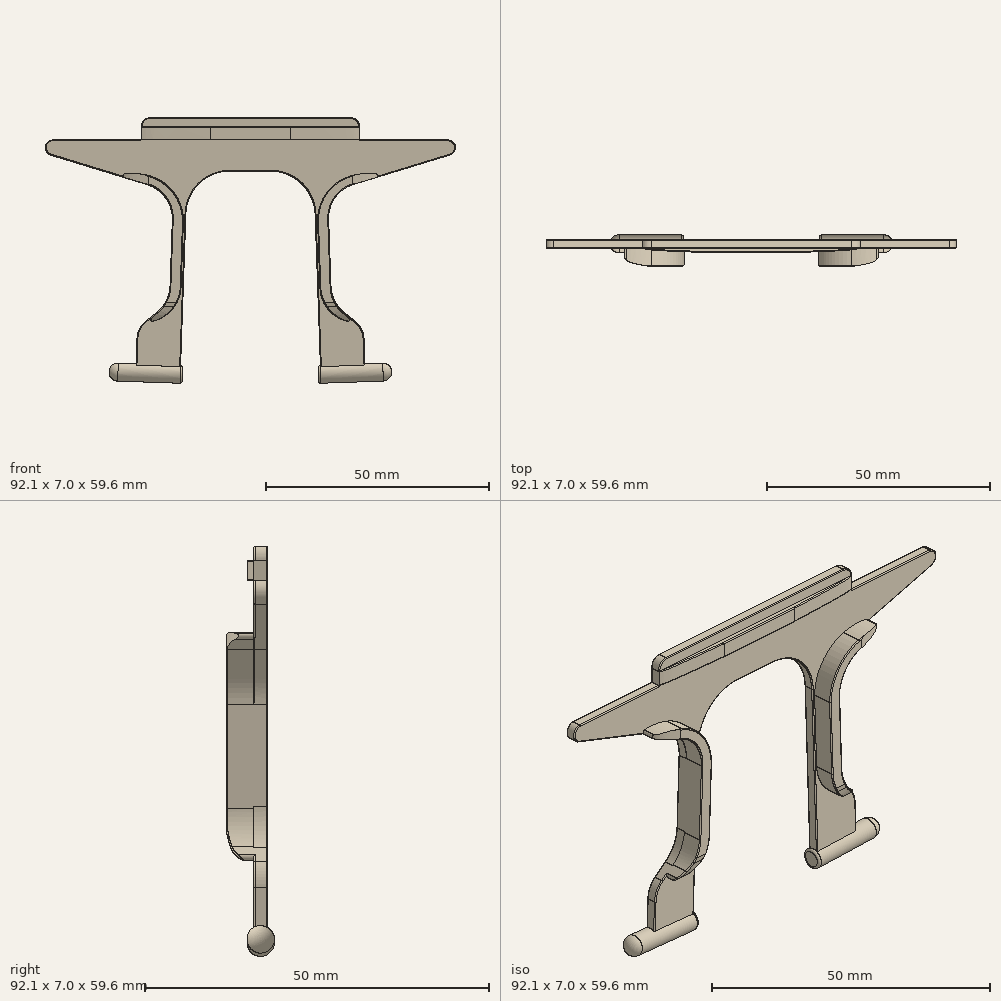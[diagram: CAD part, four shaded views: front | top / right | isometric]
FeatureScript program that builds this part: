
annotation { "Feature Type Name" : "Feature", "Feature Type Description" : "" }
export const myFeature = defineFeature(function(context is Context, id is Id, definition is map)
    precondition{}
    {
        {
            var Q0;
            Q0=qCreatedBy(makeId("Front.planeOp"),FACE);
            var sketch = newSketch(context, id + "F0", { "sketchPlane" : qUnion([Q0])});
            skLineSegment(sketch, "E0", {"start": v(24.5, 40.36) * mm, "end": v(44.5, 40.36) * mm});
            skLineSegment(sketch, "E1", {"start": v(0, 45.36) * mm, "end": v(22.5, 45.36) * mm});
            skLineSegment(sketch, "E2", {"start": v(24.5, 43.36) * mm, "end": v(24.5, 40.36) * mm});
            skPoint(sketch, "E3.visualSharp", {"position": v(24.5, 45.36) * mm});
            skArc(sketch, "E3.filletArc", {"start": v(24.5, 43.36) * mm, "mid": v(23.91, 44.77) * mm, "end": v(22.5, 45.36) * mm});
            skArc(sketch, "E4", {"start": v(44.8, 36.95) * mm, "mid": v(46, 38.99) * mm, "end": v(44.07, 40.36) * mm});
            skLineSegment(sketch, "E5", {"start": v(15.76, -12.27) * mm, "end": v(14.5, 23.7) * mm});
            skLineSegment(sketch, "E6", {"start": v(4.51, 33.36) * mm, "end": v(0, 33.36) * mm});
            skLineSegment(sketch, "E7", {"start": v(44.8, 36.95) * mm, "end": v(23.2, 30.35) * mm});
            skLineSegment(sketch, "E8", {"start": v(25.76, -11.92) * mm, "end": v(25.49, -4.2) * mm});
            skPoint(sketch, "E9.visualSharp", {"position": v(14.17, 33.36) * mm});
            skArc(sketch, "E9.filletArc", {"start": v(14.5, 23.7) * mm, "mid": v(11.46, 30.55) * mm, "end": v(4.51, 33.36) * mm});
            skLineSegment(sketch, "E10", {"start": v(25.76, -11.92) * mm, "end": v(15.76, -12.27) * mm});
            skPoint(sketch, "E11.MirrorCS.start.orphan", {"position": v(0, 45.36) * mm});
            skPoint(sketch, "E12.MirrorCS.end.orphan", {"position": v(0, 33.36) * mm});
            skLineSegment(sketch, "E13", {"start": v(0, 45.36) * mm, "end": v(0, 33.36) * mm});
            skLineSegment(sketch, "E14", {"start": v(18.06, 7.74) * mm, "end": v(17.55, 22.42) * mm});
            skPoint(sketch, "E15.visualSharp", {"position": v(17.34, 28.56) * mm});
            skArc(sketch, "E15.filletArc", {"start": v(23.2, 30.35) * mm, "mid": v(19.03, 27.35) * mm, "end": v(17.55, 22.42) * mm});
            skLineSegment(sketch, "E16", {"start": v(18.06, 7.74) * mm, "end": v(18.07, 7.54) * mm});
            skLineSegment(sketch, "E17", {"start": v(23.63, -0.5) * mm, "end": v(21.04, 1.6) * mm});
            skPoint(sketch, "E18.visualSharp", {"position": v(18.2, 3.9) * mm});
            skArc(sketch, "E18.filletArc", {"start": v(18.07, 7.54) * mm, "mid": v(18.9, 4.25) * mm, "end": v(21.04, 1.6) * mm});
            skPoint(sketch, "E19.visualSharp", {"position": v(25.4, -1.93) * mm});
            skArc(sketch, "E19.filletArc", {"start": v(25.49, -4.2) * mm, "mid": v(24.96, -2.15) * mm, "end": v(23.63, -0.5) * mm});
            skSolve(sketch);
        }
        {
            var Q0;
            Q0=makeQuery(id+"F0.imprint","IMPRINT",FACE,{"disambiguationData":[TD([[makeQuery(id+"F0.imprint","IMPRINT",EDGE,{"derivedFrom":sQuery(id+"F0.wireOp",EDGE,"E1")}),-1.0]])]});
            extrude(context, id + "F1", {"entities" : qUnion([Q0]), "depth" : 1 * mm});
        }
        {
            var Q0;
            Q0=makeQuery(id+"F1.opExtrude","SWEPT_FACE",FACE,{"disambiguationData":[OSD([sQuery(id+"F0.wireOp",EDGE,"E5")])]});
            cPlane(context, id + "F2", {"entities" : qUnion([Q0]), "cplaneType" : CPlaneType.OFFSET, "offset" : 1 * mm, "width" : 150 * mm, "height" : 150 * mm});
        }
        {
            var Q0;
            Q0=makeQuery(id+"F0.imprint","IMPRINT",FACE,{"disambiguationData":[TD([[makeQuery(id+"F0.imprint","IMPRINT",EDGE,{"derivedFrom":sQuery(id+"F0.wireOp",EDGE,"E1")}),-1.0]])]});
            extrude(context, id + "F3", {"entities" : qUnion([Q0]), "operationType" : NewBodyOperationType.ADD, "oppositeDirection" : true, "depth" : 1 * mm});
        }
        {
            var Q0;
            Q0=qCreatedBy(makeId("Front.planeOp"),FACE);
            var sketch = newSketch(context, id + "F4", { "sketchPlane" : qUnion([Q0])});
            skLineSegment(sketch, "E20.bottom", {"start": v(15.7, -10.27) * mm, "end": v(29.68, -9.79) * mm});
            skLineSegment(sketch, "E20.top", {"start": v(15.26, -12.29) * mm, "end": v(31.75, -11.71) * mm});
            skLineSegment(sketch, "E20.left", {"start": v(15.2, -10.8) * mm, "end": v(15.26, -12.29) * mm});
            skLineSegment(sketch, "E20.right", {"start": v(31.75, -11.71) * mm, "end": v(31.75, -11.71) * mm});
            skPoint(sketch, "E21.visualSharp", {"position": v(31.68, -9.72) * mm});
            skArc(sketch, "E21.filletArc", {"start": v(31.75, -11.71) * mm, "mid": v(31.12, -10.32) * mm, "end": v(29.68, -9.79) * mm});
            skPoint(sketch, "E22.visualSharp", {"position": v(15.2, -10.3) * mm});
            skArc(sketch, "E22.filletArc", {"start": v(15.7, -10.27) * mm, "mid": v(15.34, -10.43) * mm, "end": v(15.2, -10.8) * mm});
            skSolve(sketch);
        }
        {
            var Q0;
            Q0=makeQuery(id+"F4.imprint","IMPRINT",FACE,{"disambiguationData":[TD([[makeQuery(id+"F4.imprint","IMPRINT",EDGE,{"derivedFrom":sQuery(id+"F4.wireOp",EDGE,"E20.bottom")}),-1.0]])]});
            var Q1;
            Q1=sQuery(id+"F4.wireOp",EDGE,"E20.top");
            revolve(context, id + "F5", {"operationType" : NewBodyOperationType.ADD, "entities" : qUnion([Q0]), "axis" : qUnion([Q1]), "revolveType" : RevolveType.FULL});
        }
        {
            var Q0;
            Q0=qCreatedBy(makeId("Front.planeOp"),FACE);
            var sketch = newSketch(context, id + "F6", { "sketchPlane" : qUnion([Q0])});
            skLineSegment(sketch, "E23", {"start": v(27.99, 31.83) * mm, "end": v(23.2, 30.37) * mm});
            skLineSegment(sketch, "E24", {"start": v(17.9, 12.5) * mm, "end": v(17.55, 22.44) * mm});
            skArc(sketch, "E25.filletArc", {"start": v(23.2, 30.37) * mm, "mid": v(19.03, 27.36) * mm, "end": v(17.55, 22.44) * mm});
            skLineSegment(sketch, "E26", {"start": v(17.9, 12.5) * mm, "end": v(18.08, 7.32) * mm});
            skLineSegment(sketch, "E27", {"start": v(22.33, 0.55) * mm, "end": v(20.86, 1.75) * mm});
            skArc(sketch, "E28.filletArc", {"start": v(18.08, 7.32) * mm, "mid": v(18.86, 4.23) * mm, "end": v(20.86, 1.75) * mm});
            skLineSegment(sketch, "E29", {"start": v(15.05, 22.35) * mm, "end": v(15.58, 7.23) * mm});
            skLineSegment(sketch, "E30", {"start": v(17.55, 22.44) * mm, "end": v(15.05, 22.35) * mm});
            skLineSegment(sketch, "E31", {"start": v(22.5, 32.26) * mm, "end": v(22.5, 32.26) * mm});
            skLineSegment(sketch, "E32", {"start": v(15.07, 21.85) * mm, "end": v(15.05, 22.35) * mm});
            skArc(sketch, "E33.filletArc", {"start": v(22.5, 32.26) * mm, "mid": v(17.02, 28.32) * mm, "end": v(15.07, 21.85) * mm});
            skLineSegment(sketch, "E34", {"start": v(18.08, 7.32) * mm, "end": v(15.58, 7.23) * mm});
            skLineSegment(sketch, "E35", {"start": v(15.58, 7.23) * mm, "end": v(15.59, 7) * mm});
            skArc(sketch, "E36", {"start": v(15.58, 7.23) * mm, "mid": v(17.44, 2.35) * mm, "end": v(21.9, -0.37) * mm});
            skArc(sketch, "E37", {"start": v(21.9, -0.37) * mm, "mid": v(22.48, -0.08) * mm, "end": v(22.33, 0.55) * mm});
            skPoint(sketch, "E37.first.point", {"position": v(22.45, -0.13) * mm});
            skArc(sketch, "E38.trimOffspring", {"start": v(28.16, 32.74) * mm, "mid": v(25.3, 32.8) * mm, "end": v(22.5, 32.26) * mm});
            skLineSegment(sketch, "E39", {"start": v(27.99, 31.83) * mm, "end": v(28.23, 31.9) * mm});
            skArc(sketch, "E40", {"start": v(28.23, 31.9) * mm, "mid": v(28.54, 32.35) * mm, "end": v(28.16, 32.74) * mm});
            skPoint(sketch, "E40.second.point", {"position": v(28.23, 31.9) * mm});
            skSolve(sketch);
        }
        {
            var Q0;
            Q0 = qSketchRegion(id + "F6", true);
            extrude(context, id + "F7", {"entities" : qUnion([Q0]), "operationType" : NewBodyOperationType.ADD, "depth" : 5 * mm});
        }
        {
            var Q0;
            Q0=qCreatedBy(makeId("Right.planeOp"),FACE);
            var sketch = newSketch(context, id + "F8", { "sketchPlane" : qUnion([Q0])});
            skFitSpline(sketch, "E41", {"points": [v(-4.8, 2.94) * mm, v(-3.88, 0.66) * mm, v(-2.13, -0.5) * mm], "startDerivative": vector(1.29, -4.9) * mm, "endDerivative": vector(4.1, -1.93) * mm});
            skLineSegment(sketch, "E42", {"start": v(-4.8, 2.94) * mm, "end": v(-5.4, 5.71) * mm});
            skLineSegment(sketch, "E43", {"start": v(-5.4, 5.71) * mm, "end": v(-6.33, 5.51) * mm});
            skLineSegment(sketch, "E44", {"start": v(-6.33, 5.51) * mm, "end": v(-6.33, 2.04) * mm});
            skLineSegment(sketch, "E45", {"start": v(-6.33, 2.04) * mm, "end": v(-6.33, -1.36) * mm});
            skLineSegment(sketch, "E46", {"start": v(-6.33, -1.36) * mm, "end": v(-2.06, -1.36) * mm});
            skLineSegment(sketch, "E47", {"start": v(-2.06, -1.36) * mm, "end": v(-2.13, -0.5) * mm});
            skSolve(sketch);
        }
        {
            var Q0;
            Q0=makeQuery(id+"F8.imprint","IMPRINT",FACE,{"disambiguationData":[TD([[makeQuery(id+"F8.imprint","IMPRINT",EDGE,{"derivedFrom":sQuery(id+"F8.wireOp",EDGE,"E41")}),-1.0]])]});
            extrude(context, id + "F9", {"entities" : qUnion([Q0]), "operationType" : NewBodyOperationType.REMOVE, "depth" : 25 * mm});
        }
        {
            var Q0;
            Q0=qCreatedBy(makeId("Top.planeOp"),FACE);
            var sketch = newSketch(context, id + "F10", { "sketchPlane" : qUnion([Q0])});
            skFitSpline(sketch, "E48", {"points": [v(28.64, -3.11) * mm, v(26.82, -4.28) * mm, v(21.34, -5.17) * mm, v(21.32, -5.17) * mm], "startDerivative": vector(-3.06, -3.38) * mm, "endDerivative": vector(-0.28, 0.04) * mm});
            skLineSegment(sketch, "E49", {"start": v(21.34, -5.17) * mm, "end": v(21.34, -6.23) * mm});
            skLineSegment(sketch, "E50", {"start": v(21.34, -6.23) * mm, "end": v(29, -6.23) * mm});
            skLineSegment(sketch, "E51", {"start": v(29, -6.23) * mm, "end": v(29.97, -3.8) * mm});
            skLineSegment(sketch, "E52", {"start": v(29.97, -3.8) * mm, "end": v(29.39, -3.18) * mm});
            skLineSegment(sketch, "E53", {"start": v(29.39, -3.18) * mm, "end": v(28.64, -3.11) * mm});
            skSolve(sketch);
        }
        {
            var Q0;
            {var subQ0=sQuery(id+"F10.wireOp",EDGE,"E49");Q0=makeQuery(id+"F10.imprint","IMPRINT",FACE,{"disambiguationData":[TD([[makeQuery(id+"F10.imprint","IMPRINT",EDGE,{"derivedFrom":subQ0}),1.0]])]});}
            extrude(context, id + "F11", {"entities" : qUnion([Q0]), "operationType" : NewBodyOperationType.REMOVE, "depth" : 35 * mm});
        }
        {
            var Q0;
            Q0=makeQuery(id+"F7.opExtrude","CAP_EDGE",EDGE,{"disambiguationData":[OSD([sQuery(id+"F6.wireOp",EDGE,"E33.filletArc")])],"isStart":false});
            fillet(context, id + "F12", {"entities" : qUnion([Q0]), "radius" : 0.2 * mm, "tangentPropagation" : true, "allowEdgeOverflow" : false});
        }
        {
            var Q0;
            Q0=qCreatedBy(makeId("Right.planeOp"),FACE);
            var sketch = newSketch(context, id + "F13", { "sketchPlane" : qUnion([Q0])});
            skLineSegment(sketch, "E54", {"start": v(0, 43.36) * mm, "end": v(0, 41.86) * mm});
            skLineSegment(sketch, "E55.MirrorCS", {"start": v(0, 41.1) * mm, "end": v(0, 41.86) * mm});
            skLineSegment(sketch, "E56.MirrorCS", {"start": v(-1.5, 40.36) * mm, "end": v(0, 40.36) * mm});
            skLineSegment(sketch, "E57.MirrorCS", {"start": v(-2, 41.86) * mm, "end": v(-2, 41.6) * mm});
            skLineSegment(sketch, "E58.MirrorCS", {"start": v(-1.5, 43.36) * mm, "end": v(0, 43.36) * mm});
            skLineSegment(sketch, "E59.MirrorCS", {"start": v(-2, 42.6) * mm, "end": v(-2, 42.86) * mm});
            skLineSegment(sketch, "E60", {"start": v(-2, 42.6) * mm, "end": v(-2, 41.86) * mm});
            skLineSegment(sketch, "E61", {"start": v(-2, 41.6) * mm, "end": v(-2, 40.86) * mm});
            skLineSegment(sketch, "E62", {"start": v(0, 40.36) * mm, "end": v(0, 41.1) * mm});
            skLineSegment(sketch, "E63", {"start": v(-1.5, 43.36) * mm, "end": v(-2, 43.36) * mm});
            skLineSegment(sketch, "E64", {"start": v(-2, 43.36) * mm, "end": v(-2, 42.86) * mm});
            skLineSegment(sketch, "E65", {"start": v(-2, 40.86) * mm, "end": v(-2, 40.36) * mm});
            skLineSegment(sketch, "E66", {"start": v(-2, 40.36) * mm, "end": v(-1.5, 40.36) * mm});
            skSolve(sketch);
        }
        {
            var Q0;
            {var subQ0=sQuery(id+"F0.wireOp",EDGE,"E1");Q0=makeQuery(id+"F3.boolean.opBoolean","MERGE",FACE,{"derivedFrom":[makeQuery(id+"F1.opExtrude","SWEPT_FACE",FACE,{"disambiguationData":[OSD([subQ0])]}),makeQuery(id+"F3.opExtrude","SWEPT_FACE",FACE,{"disambiguationData":[OSD([subQ0])]})]});}
            cPlane(context, id + "F14", {"entities" : qUnion([Q0]), "cplaneType" : CPlaneType.OFFSET, "offset" : 0 * mm, "width" : 150 * mm, "height" : 150 * mm});
        }
        {
            var Q0;
            Q0=qCreatedBy(id+"F14.planeOp",FACE);
            var sketch = newSketch(context, id + "F15", { "sketchPlane" : qUnion([Q0])});
            skFitSpline(sketch, "E67.MirrorCS", {"points": [v(24.5, -1) * mm, v(21.47, -1.45) * mm, v(5.2, -2.1) * mm, v(5.2, -2.1) * mm], "startDerivative": vector(-5.5, -1.5) * mm, "endDerivative": vector(0, 0.09) * mm});
            skLineSegment(sketch, "E68.MirrorCS", {"start": v(5.94, -2.88) * mm, "end": v(18.16, -2.88) * mm});
            skLineSegment(sketch, "E69.MirrorCS", {"start": v(18.16, -2.88) * mm, "end": v(22.17, -2.88) * mm});
            skLineSegment(sketch, "E70.MirrorCS", {"start": v(22.17, -2.88) * mm, "end": v(25.12, -2.55) * mm});
            skLineSegment(sketch, "E71.MirrorCS", {"start": v(25.12, -2.55) * mm, "end": v(25, -1.52) * mm});
            skLineSegment(sketch, "E72.MirrorCS", {"start": v(24.5, -1) * mm, "end": v(25, -1.52) * mm});
            skLineSegment(sketch, "E73.MirrorCS", {"start": v(5.2, -2.1) * mm, "end": v(5.94, -2.88) * mm});
            skSolve(sketch);
        }
        {
            var Q0;
            Q0=makeQuery(id+"F13.imprint","IMPRINT",FACE,{"disambiguationData":[TD([[makeQuery(id+"F13.imprint","IMPRINT",EDGE,{"derivedFrom":sQuery(id+"F13.wireOp",EDGE,"E54")}),-1.0]])]});
            extrude(context, id + "F16", {"entities" : qUnion([Q0]), "operationType" : NewBodyOperationType.ADD, "depth" : 24.5 * mm});
        }
        {
            var Q0;
            Q0 = qSketchRegion(id + "F15", true);
            extrude(context, id + "F17", {"entities" : qUnion([Q0]), "operationType" : NewBodyOperationType.REMOVE, "oppositeDirection" : true, "depth" : 5 * mm});
        }
        {
            var Q0;
            Q0=makeQuery(id+"F1.opExtrude","CAP_EDGE",EDGE,{"disambiguationData":[OSD([sQuery(id+"F0.wireOp",EDGE,"E1")])],"isStart":false});
            var Q1;
            Q1=makeQuery(id+"F16.opExtrude","SWEPT_EDGE",EDGE,{"disambiguationData":[OSD([sQuery(id+"F13.wireOp",EDGE,"E63"),sQuery(id+"F13.wireOp",EDGE,"E64")])]});
            var Q2;
            Q2=makeQuery(id+"F1.opExtrude","CAP_EDGE",EDGE,{"disambiguationData":[OSD([sQuery(id+"F0.wireOp",EDGE,"E3.filletArc")])],"isStart":false});
            var Q3;
            Q3=makeQuery(id+"F16.opExtrude","SWEPT_EDGE",EDGE,{"disambiguationData":[OSD([sQuery(id+"F13.wireOp",EDGE,"E65"),sQuery(id+"F13.wireOp",EDGE,"E66")])]});
            var Q4;
            Q4=makeQuery(id+"F1.opExtrude","CAP_EDGE",EDGE,{"disambiguationData":[OSD([sQuery(id+"F0.wireOp",EDGE,"E6")])],"isStart":false});
            var Q5;
            Q5=makeQuery(id+"F1.opExtrude","CAP_EDGE",EDGE,{"disambiguationData":[OSD([sQuery(id+"F0.wireOp",EDGE,"E0")])],"isStart":false});
            var Q6;
            Q6=makeQuery(id+"F1.opExtrude","CAP_EDGE",EDGE,{"disambiguationData":[OSD([sQuery(id+"F0.wireOp",EDGE,"E4")])],"isStart":false});
            var Q7;
            {var subQ0=sQuery(id+"F0.wireOp",EDGE,"E7");Q7=makeQuery(id+"F11.boolean.opBoolean","INTERSECT",EDGE,{"derivedFrom":[makeQuery(id+"F7.boolean.opBoolean","MERGE",FACE,{"derivedFrom":[makeQuery(id+"F3.boolean.opBoolean","MERGE",FACE,{"derivedFrom":[makeQuery(id+"F1.opExtrude","SWEPT_FACE",FACE,{"disambiguationData":[OSD([subQ0])]}),makeQuery(id+"F3.opExtrude","SWEPT_FACE",FACE,{"disambiguationData":[OSD([subQ0])]})]}),makeQuery(id+"F7.opExtrude","SWEPT_FACE",FACE,{"disambiguationData":[OSD([sQuery(id+"F6.wireOp",EDGE,"E23"),sQuery(id+"F6.wireOp",EDGE,"E39")])]})]}),makeQuery(id+"F11.opExtrude","SWEPT_FACE",FACE,{"disambiguationData":[OSD([sQuery(id+"F10.wireOp",EDGE,"E48")])]})]});}
            var Q8;
            Q8=makeQuery(id+"F7.opExtrude","CAP_EDGE",EDGE,{"disambiguationData":[OSD([sQuery(id+"F6.wireOp",EDGE,"E25.filletArc")])],"isStart":false});
            var Q9;
            Q9=makeQuery(id+"F7.opExtrude","CAP_EDGE",EDGE,{"disambiguationData":[OSD([sQuery(id+"F6.wireOp",EDGE,"E29"),sQuery(id+"F6.wireOp",EDGE,"E32")])],"isStart":false});
            var Q10;
            Q10=makeQuery(id+"F9.boolean.opBoolean","INTERSECT",EDGE,{"derivedFrom":[makeQuery(id+"F7.opExtrude","SWEPT_FACE",FACE,{"disambiguationData":[OSD([sQuery(id+"F6.wireOp",EDGE,"E28.filletArc")])]}),makeQuery(id+"F9.opExtrude","SWEPT_FACE",FACE,{"disambiguationData":[OSD([sQuery(id+"F8.wireOp",EDGE,"E42")])]})]});
            var Q11;
            {var subQ0=sQuery(id+"F0.wireOp",EDGE,"E17");Q11=makeQuery(id+"F9.boolean.opBoolean","INTERSECT",EDGE,{"derivedFrom":[makeQuery(id+"F7.boolean.opBoolean","MERGE",FACE,{"derivedFrom":[makeQuery(id+"F3.boolean.opBoolean","MERGE",FACE,{"derivedFrom":[makeQuery(id+"F1.opExtrude","SWEPT_FACE",FACE,{"disambiguationData":[OSD([subQ0])]}),makeQuery(id+"F3.opExtrude","SWEPT_FACE",FACE,{"disambiguationData":[OSD([subQ0])]})]}),makeQuery(id+"F7.opExtrude","SWEPT_FACE",FACE,{"disambiguationData":[OSD([sQuery(id+"F6.wireOp",EDGE,"E27")])]})]}),makeQuery(id+"F9.opExtrude","SWEPT_FACE",FACE,{"disambiguationData":[OSD([sQuery(id+"F8.wireOp",EDGE,"E41")])]})]});}
            var Q12;
            Q12=makeQuery(id+"F9.boolean.opBoolean","INTERSECT",EDGE,{"derivedFrom":[makeQuery(id+"F7.opExtrude","SWEPT_FACE",FACE,{"disambiguationData":[OSD([sQuery(id+"F6.wireOp",EDGE,"E36")])]}),makeQuery(id+"F9.opExtrude","SWEPT_FACE",FACE,{"disambiguationData":[OSD([sQuery(id+"F8.wireOp",EDGE,"E41")])]})]});
            var Q13;
            Q13=makeQuery(id+"F9.boolean.opBoolean","INTERSECT",EDGE,{"derivedFrom":[makeQuery(id+"F7.opExtrude","SWEPT_FACE",FACE,{"disambiguationData":[OSD([sQuery(id+"F6.wireOp",EDGE,"E36")])]}),makeQuery(id+"F9.opExtrude","SWEPT_FACE",FACE,{"disambiguationData":[OSD([sQuery(id+"F8.wireOp",EDGE,"E42")])]})]});
            var Q14;
            Q14=makeQuery(id+"F1.opExtrude","CAP_EDGE",EDGE,{"disambiguationData":[OSD([sQuery(id+"F0.wireOp",EDGE,"E19.filletArc")])],"isStart":false});
            var Q15;
            Q15=makeQuery(id+"F1.opExtrude","CAP_EDGE",EDGE,{"disambiguationData":[OSD([sQuery(id+"F0.wireOp",EDGE,"E17")])],"isStart":false});
            var Q16;
            Q16=makeQuery(id+"F1.opExtrude","CAP_EDGE",EDGE,{"disambiguationData":[OSD([sQuery(id+"F0.wireOp",EDGE,"E8")])],"isStart":false});
            var Q17;
            Q17=makeQuery(id+"F3.opExtrude","CAP_EDGE",EDGE,{"disambiguationData":[OSD([sQuery(id+"F0.wireOp",EDGE,"E5")])],"isStart":false});
            var Q18;
            Q18=makeQuery(id+"F3.opExtrude","CAP_EDGE",EDGE,{"disambiguationData":[OSD([sQuery(id+"F0.wireOp",EDGE,"E1")])],"isStart":false});
            var Q19;
            Q19=makeQuery(id+"F3.opExtrude","CAP_EDGE",EDGE,{"disambiguationData":[OSD([sQuery(id+"F0.wireOp",EDGE,"E0")])],"isStart":false});
            var Q20;
            Q20=makeQuery(id+"F3.opExtrude","CAP_EDGE",EDGE,{"disambiguationData":[OSD([sQuery(id+"F0.wireOp",EDGE,"E4")])],"isStart":false});
            fillet(context, id + "F18", {"entities" : qUnion([Q0, Q1, Q2, Q3, Q4, Q5, Q6, Q7, Q8, Q9, Q10, Q11, Q12, Q13, Q14, Q15, Q16, Q17, Q18, Q19, Q20]), "radius" : 0.2 * mm, "tangentPropagation" : true, "allowEdgeOverflow" : false});
        }
        {
            var Q0;
            Q0=makeQuery(id+"F17.boolean.opBoolean","INTERSECT",EDGE,{"derivedFrom":[makeQuery(id+"F16.opExtrude","SWEPT_FACE",FACE,{"disambiguationData":[OSD([sQuery(id+"F13.wireOp",EDGE,"E58.MirrorCS"),sQuery(id+"F13.wireOp",EDGE,"E63")])]}),makeQuery(id+"F17.opExtrude","SWEPT_FACE",FACE,{"disambiguationData":[OSD([sQuery(id+"F15.wireOp",EDGE,"E67.MirrorCS")])]})]});
            var Q1;
            Q1=makeQuery(id+"F17.boolean.opBoolean","COPY",EDGE,{"derivedFrom":makeQuery(id+"F17.opExtrude","CAP_EDGE",EDGE,{"disambiguationData":[OSD([sQuery(id+"F15.wireOp",EDGE,"E67.MirrorCS")])],"isStart":false})});
            fillet(context, id + "F19", {"entities" : qUnion([Q0, Q1]), "radius" : 0.19 * mm, "tangentPropagation" : true, "allowEdgeOverflow" : false});
        }
        {
            var Q0;
            Q0=makeQuery(id+"F1.opExtrude","SWEPT_BODY",BODY,{"disambiguationData":[OSD([sQuery(id+"F0.wireOp",EDGE,"E0"),sQuery(id+"F0.wireOp",EDGE,"E1"),sQuery(id+"F0.wireOp",EDGE,"E2"),sQuery(id+"F0.wireOp",EDGE,"E3.filletArc"),sQuery(id+"F0.wireOp",EDGE,"E4"),sQuery(id+"F0.wireOp",EDGE,"E5"),sQuery(id+"F0.wireOp",EDGE,"E6"),sQuery(id+"F0.wireOp",EDGE,"E7"),sQuery(id+"F0.wireOp",EDGE,"E8"),sQuery(id+"F0.wireOp",EDGE,"E9.filletArc"),sQuery(id+"F0.wireOp",EDGE,"E10"),sQuery(id+"F0.wireOp",EDGE,"E13"),sQuery(id+"F0.wireOp",EDGE,"E14"),sQuery(id+"F0.wireOp",EDGE,"E15.filletArc"),sQuery(id+"F0.wireOp",EDGE,"E16"),sQuery(id+"F0.wireOp",EDGE,"E17"),sQuery(id+"F0.wireOp",EDGE,"E18.filletArc"),sQuery(id+"F0.wireOp",EDGE,"E19.filletArc")])]});
            var Q1;
            {var subQ0=sQuery(id+"F0.wireOp",EDGE,"E13");Q1=makeQuery(id+"F16.boolean.opBoolean","MERGE",FACE,{"derivedFrom":[makeQuery(id+"F3.boolean.opBoolean","MERGE",FACE,{"derivedFrom":[makeQuery(id+"F1.opExtrude","SWEPT_FACE",FACE,{"disambiguationData":[OSD([subQ0])]}),makeQuery(id+"F3.opExtrude","SWEPT_FACE",FACE,{"disambiguationData":[OSD([subQ0])]})]}),makeQuery(id+"F16.opExtrude","CAP_FACE",FACE,{"disambiguationData":[OSD([sQuery(id+"F13.wireOp",EDGE,"E54"),sQuery(id+"F13.wireOp",EDGE,"E55.MirrorCS"),sQuery(id+"F13.wireOp",EDGE,"E56.MirrorCS"),sQuery(id+"F13.wireOp",EDGE,"E57.MirrorCS"),sQuery(id+"F13.wireOp",EDGE,"E59.MirrorCS"),sQuery(id+"F13.wireOp",EDGE,"E58.MirrorCS"),sQuery(id+"F13.wireOp",EDGE,"E60"),sQuery(id+"F13.wireOp",EDGE,"E61"),sQuery(id+"F13.wireOp",EDGE,"E62"),sQuery(id+"F13.wireOp",EDGE,"E63"),sQuery(id+"F13.wireOp",EDGE,"E64"),sQuery(id+"F13.wireOp",EDGE,"E65"),sQuery(id+"F13.wireOp",EDGE,"E66")])],"isStart":true})]});}
            mirror(context, id + "F20", {"operationType" : NewBodyOperationType.ADD, "entities" : qUnion([Q0]), "mirrorPlane" : qUnion([Q1])});
        }
    });
